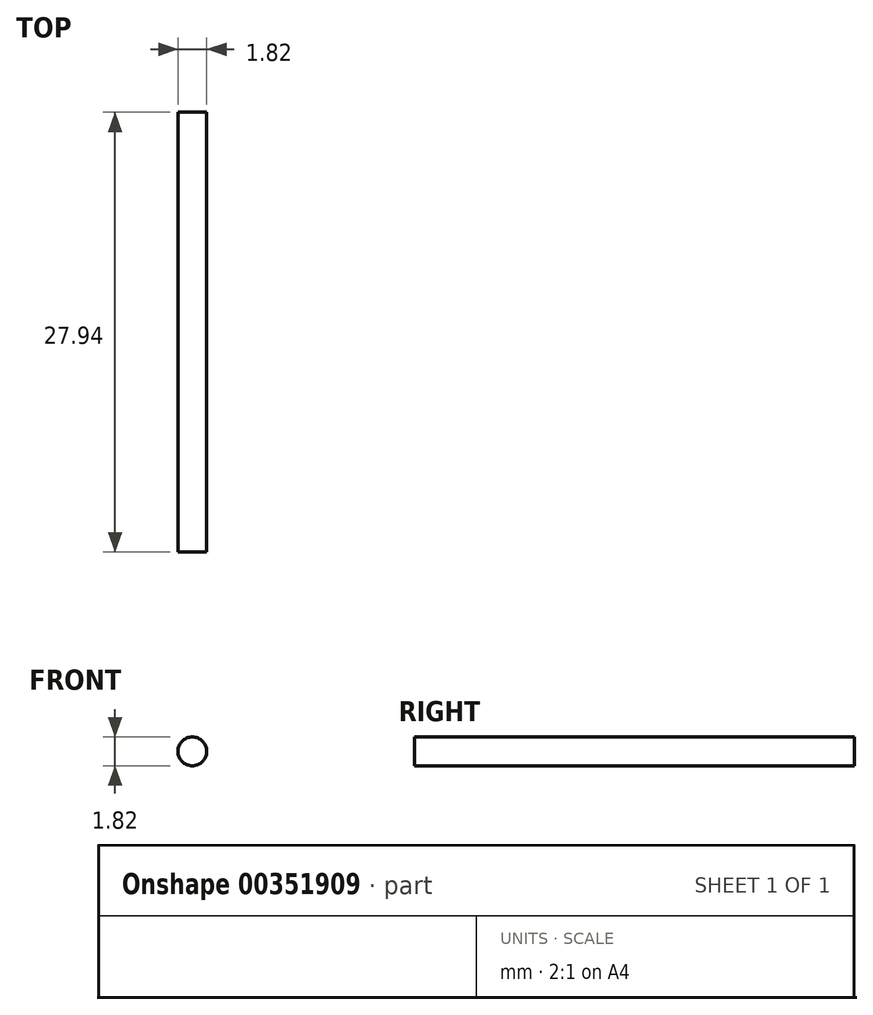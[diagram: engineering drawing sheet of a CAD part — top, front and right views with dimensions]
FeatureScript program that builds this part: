
annotation { "Feature Type Name" : "Feature", "Feature Type Description" : "" }
export const myFeature = defineFeature(function(context is Context, id is Id, definition is map)
    precondition{}
    {
        {
            var Q0;
            Q0=qCreatedBy(makeId("Front.planeOp"),FACE);
            var sketch = newSketch(context, id + "F0", { "sketchPlane" : qUnion([Q0])});
            skCircle(sketch, "E0", {"center": v(0, 0) * mm, "radius": 0.91 * mm});
            skSolve(sketch);
        }
        {
            var Q0;
            Q0 = qSketchRegion(id + "F0", true);
            extrude(context, id + "F1", {"entities" : qUnion([Q0]), "depth" : 27.94 * mm});
        }
    });
